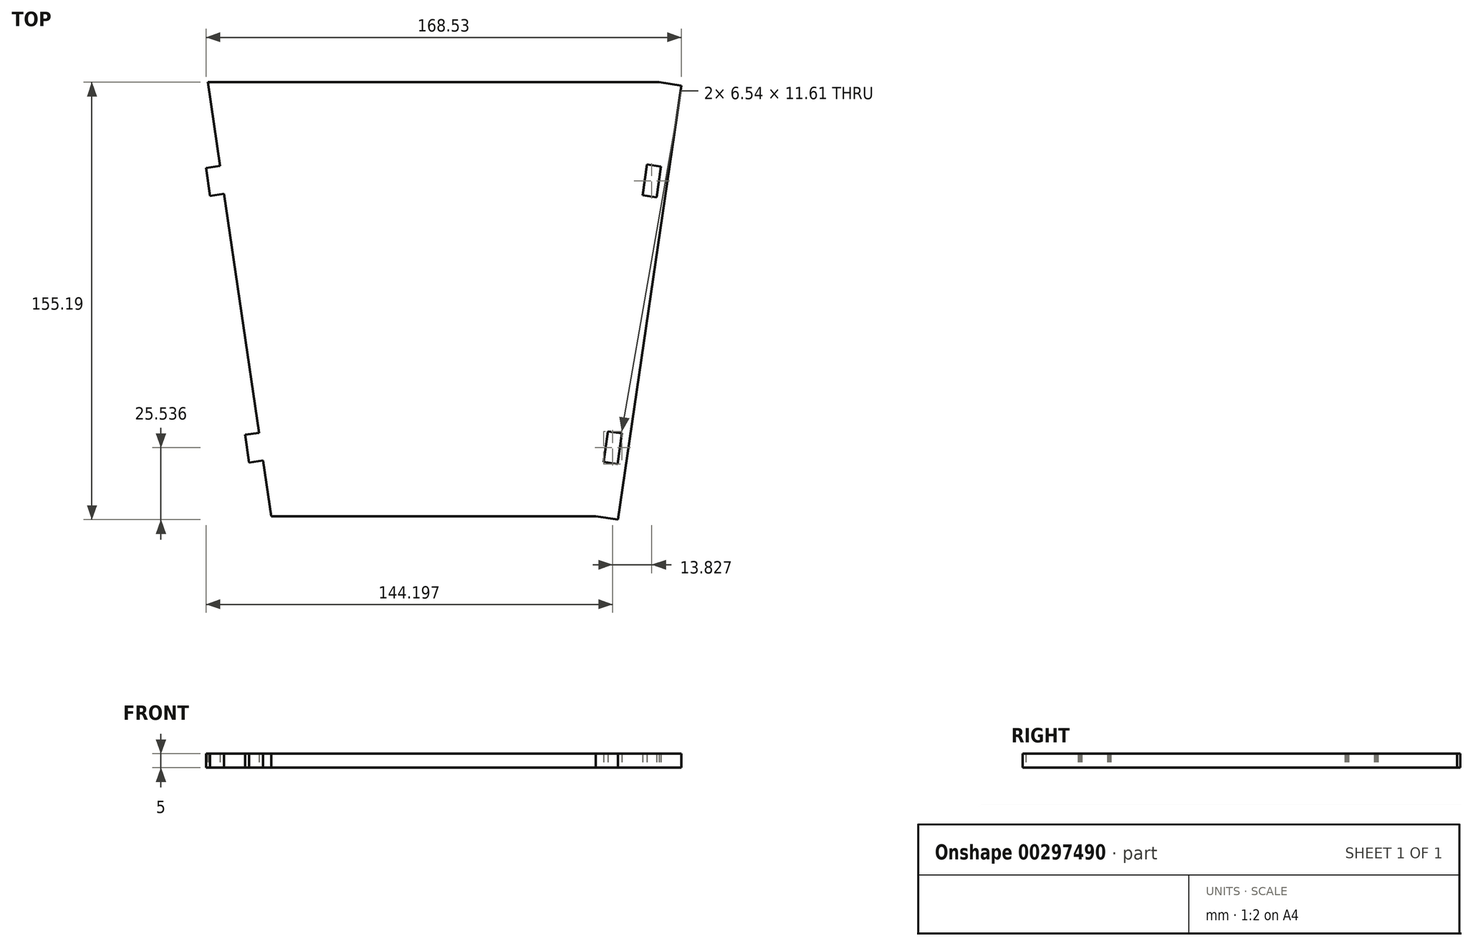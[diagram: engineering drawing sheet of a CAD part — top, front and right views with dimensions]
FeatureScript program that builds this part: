
annotation { "Feature Type Name" : "Feature", "Feature Type Description" : "" }
export const myFeature = defineFeature(function(context is Context, id is Id, definition is map)
    precondition{}
    {
        {
            var Q0;
            Q0=qCreatedBy(makeId("Top.planeOp"),FACE);
            var sketch = newSketch(context, id + "F0", { "sketchPlane" : qUnion([Q0])});
            skLineSegment(sketch, "E0", {"start": v(-80, 154.03) * mm, "end": v(80, 154.03) * mm});
            skLineSegment(sketch, "E1", {"start": v(57.5, 0) * mm, "end": v(-57.5, 0) * mm});
            skLineSegment(sketch, "E2", {"start": v(-57.5, 0) * mm, "end": v(-60.4, 19.79) * mm});
            skPoint(sketch, "E3", {"position": v(0, 0) * mm});
            skLineSegment(sketch, "E4", {"start": v(-75.66, 124.34) * mm, "end": v(-80.61, 123.62) * mm});
            skLineSegment(sketch, "E5", {"start": v(-80.61, 123.62) * mm, "end": v(-79.17, 113.73) * mm});
            skLineSegment(sketch, "E6", {"start": v(-79.17, 113.73) * mm, "end": v(-74.22, 114.45) * mm});
            skLineSegment(sketch, "E7", {"start": v(-61.84, 29.68) * mm, "end": v(-66.78, 28.96) * mm});
            skLineSegment(sketch, "E8", {"start": v(-66.78, 28.96) * mm, "end": v(-65.34, 19.07) * mm});
            skLineSegment(sketch, "E9", {"start": v(-65.34, 19.07) * mm, "end": v(-60.4, 19.79) * mm});
            skPoint(sketch, "E10", {"position": v(60.32, 19.3) * mm});
            skLineSegment(sketch, "E11", {"start": v(60.32, 19.3) * mm, "end": v(65.27, 18.57) * mm});
            skLineSegment(sketch, "E12", {"start": v(65.27, 18.57) * mm, "end": v(66.86, 29.46) * mm});
            skLineSegment(sketch, "E13", {"start": v(66.86, 29.46) * mm, "end": v(61.9, 30.18) * mm});
            skLineSegment(sketch, "E14", {"start": v(74.15, 113.95) * mm, "end": v(79.1, 113.23) * mm});
            skLineSegment(sketch, "E15", {"start": v(79.1, 113.23) * mm, "end": v(80.68, 124.12) * mm});
            skLineSegment(sketch, "E16", {"start": v(80.68, 124.12) * mm, "end": v(75.74, 124.84) * mm});
            skLineSegment(sketch, "E17.trimOffspring", {"start": v(-75.66, 124.34) * mm, "end": v(-80, 154.03) * mm});
            skLineSegment(sketch, "E18.trimOffspring", {"start": v(-61.84, 29.68) * mm, "end": v(-74.22, 114.45) * mm});
            skLineSegment(sketch, "E19.trimOffspring", {"start": v(75.74, 124.84) * mm, "end": v(74.15, 113.95) * mm});
            skLineSegment(sketch, "E20.trimOffspring", {"start": v(61.9, 30.18) * mm, "end": v(60.32, 19.3) * mm});
            skLineSegment(sketch, "E21", {"start": v(80, 154.03) * mm, "end": v(87.92, 152.87) * mm});
            skLineSegment(sketch, "E22", {"start": v(57.5, 0) * mm, "end": v(65.42, -1.16) * mm});
            skLineSegment(sketch, "E23", {"start": v(87.92, 152.87) * mm, "end": v(65.42, -1.16) * mm});
            skSolve(sketch);
        }
        {
            var Q0;
            Q0=makeQuery(id+"F0.imprint","IMPRINT",FACE,{"disambiguationData":[TD([[makeQuery(id+"F0.imprint","IMPRINT",EDGE,{"derivedFrom":sQuery(id+"F0.wireOp",EDGE,"E0")}),-1.0]])]});
            extrude(context, id + "F1", {"entities" : qUnion([Q0]), "depth" : 5 * mm});
        }
    });
